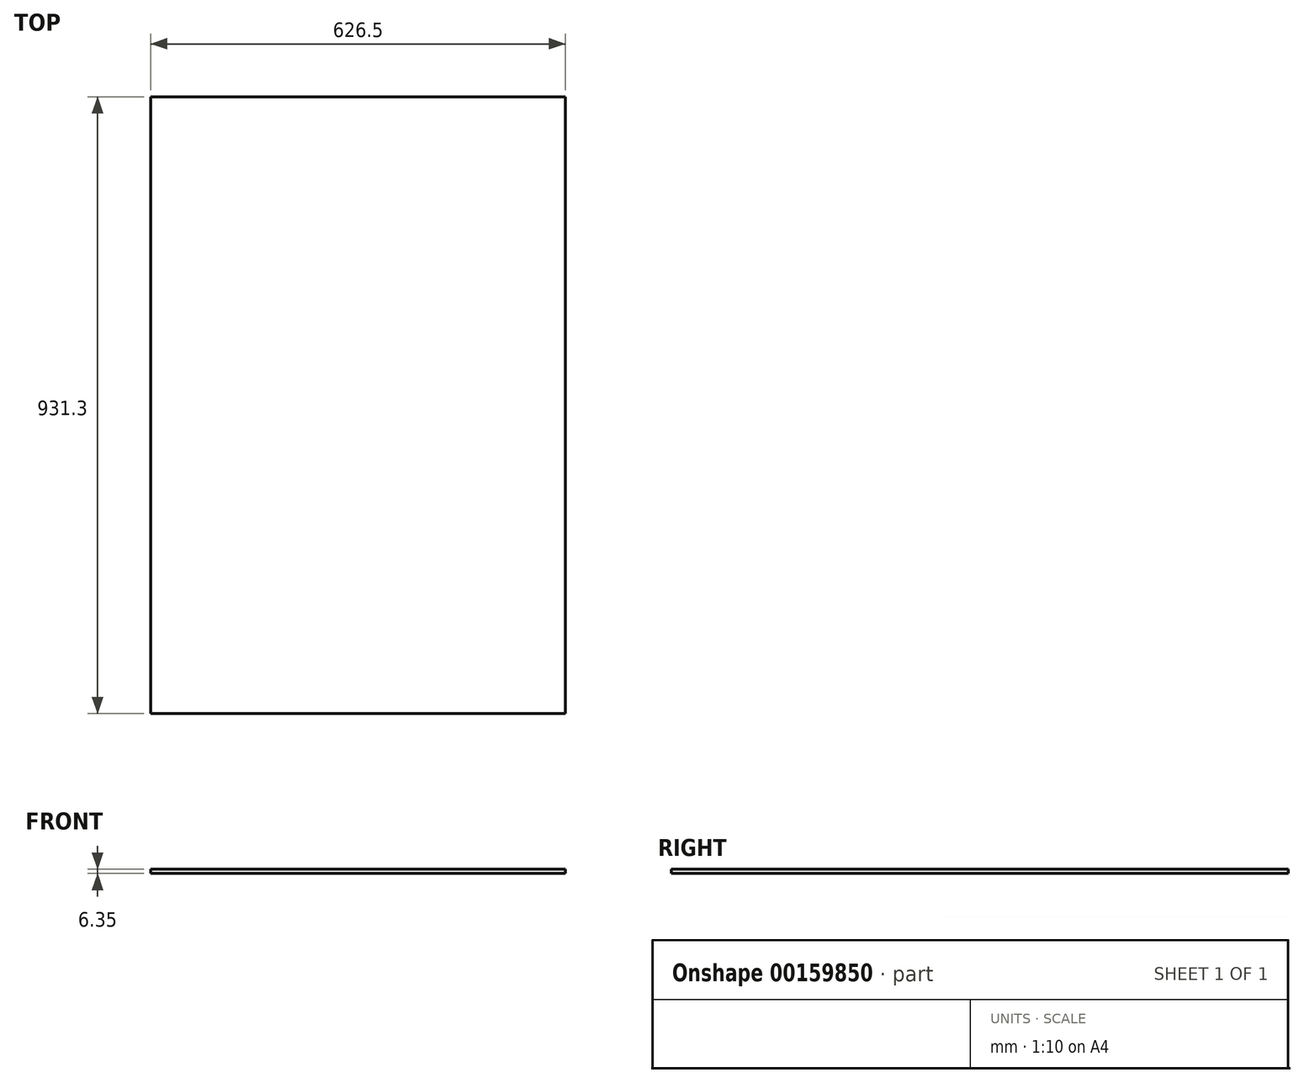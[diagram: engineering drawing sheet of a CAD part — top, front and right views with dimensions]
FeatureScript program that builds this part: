
annotation { "Feature Type Name" : "Feature", "Feature Type Description" : "" }
export const myFeature = defineFeature(function(context is Context, id is Id, definition is map)
    precondition{}
    {
        {
            var Q0;
            Q0=qCreatedBy(makeId("Top.planeOp"),FACE);
            var sketch = newSketch(context, id + "F0", { "sketchPlane" : qUnion([Q0])});
            skLineSegment(sketch, "E0.bottom", {"start": v(313.25, -465.65) * mm, "end": v(-313.25, -465.65) * mm});
            skLineSegment(sketch, "E0.top", {"start": v(313.25, 465.65) * mm, "end": v(-313.25, 465.65) * mm});
            skLineSegment(sketch, "E0.left", {"start": v(313.25, -465.65) * mm, "end": v(313.25, 465.65) * mm});
            skLineSegment(sketch, "E0.right", {"start": v(-313.25, -465.65) * mm, "end": v(-313.25, 465.65) * mm});
            skPoint(sketch, "E0.middle", {"position": v(0, 0) * mm});
            skSolve(sketch);
        }
        {
            var Q0;
            Q0 = qSketchRegion(id + "F0", true);
            extrude(context, id + "F1", {"entities" : qUnion([Q0]), "depth" : 6.35 * mm});
        }
    });
